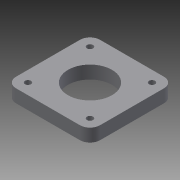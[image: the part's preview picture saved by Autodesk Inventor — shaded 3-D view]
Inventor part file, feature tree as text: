
AUTODESK INVENTOR PART (.ipt)
format: ipt  version: 2013 (Build 170138000, 138)  size: 95,744 bytes
history: native  units: mm
features: extrude x1, fillet x1, sketch x1
ambient origin geometry x8: Origin, YZ Plane, XZ Plane, XY Plane, X Axis, Y Axis, Z Axis, Center Point
bodies: Solid1 (feature_tree)
feature tree (3):
  extrude  "Extrusion1"  Depth=22.0mm
  fillet  "Fillet1"  Radius=31.0mm
  sketch  "Sketch1"  dims[d0=42.0mm d1=22.0mm d2=31.0mm d3=3.0mm d4=6.477mm d5=0.0mm d6=5.0mm]
